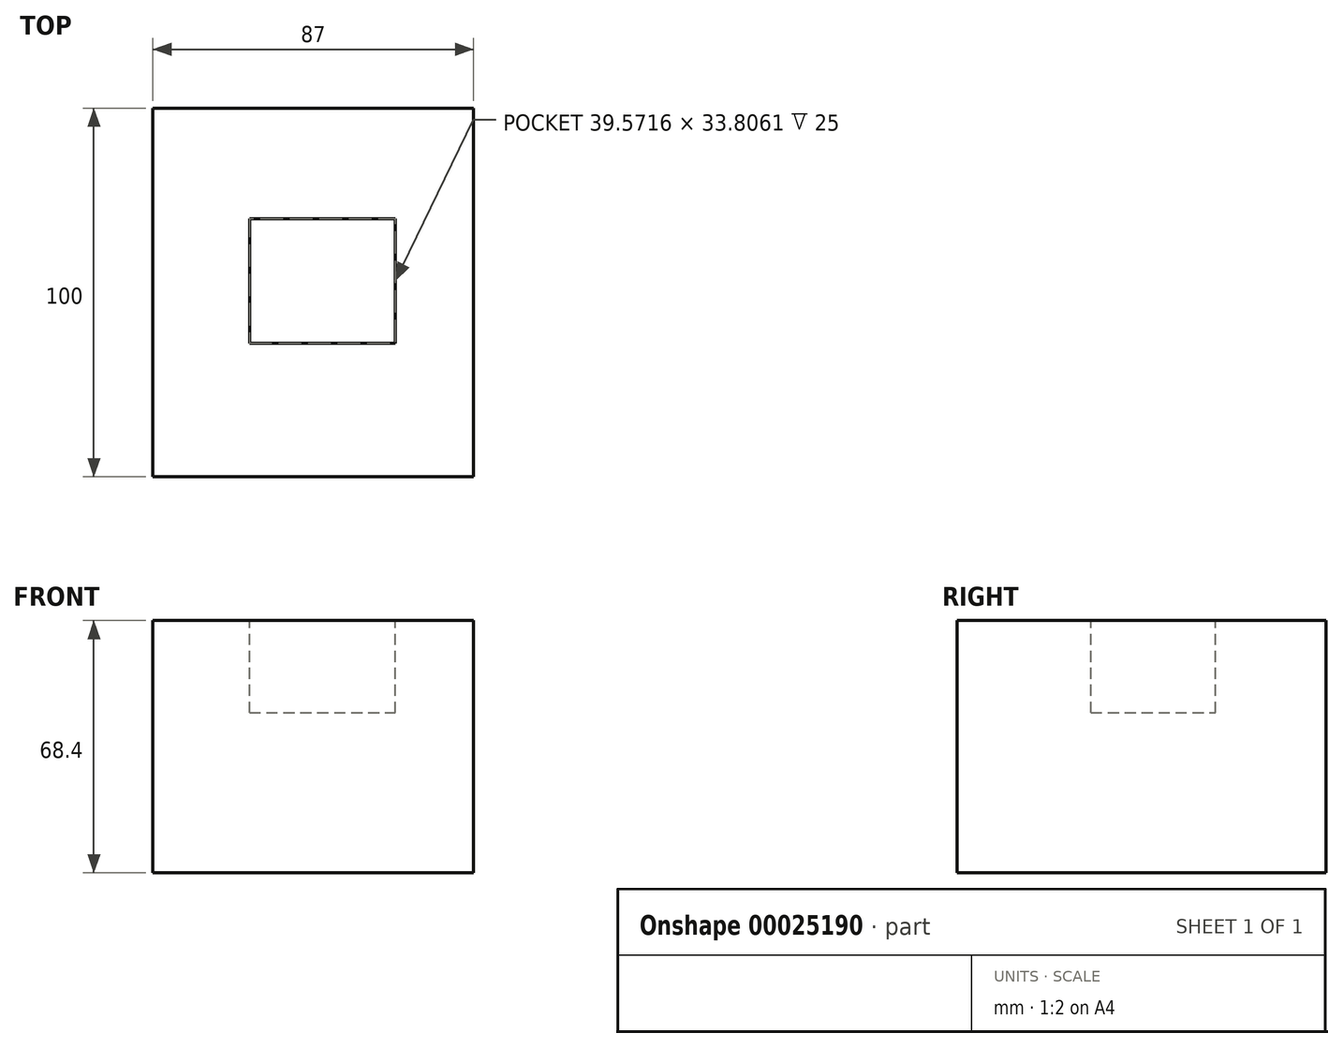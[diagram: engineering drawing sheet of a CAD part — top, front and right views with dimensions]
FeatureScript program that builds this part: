
annotation { "Feature Type Name" : "Feature", "Feature Type Description" : "" }
export const myFeature = defineFeature(function(context is Context, id is Id, definition is map)
    precondition{}
    {
        {
            var Q0;
            Q0=qCreatedBy(makeId("Front.planeOp"),FACE);
            var sketch = newSketch(context, id + "F0", { "sketchPlane" : qUnion([Q0])});
            skLineSegment(sketch, "E0.bottom", {"start": v(-44.81, -26.6) * mm, "end": v(42.2, -26.6) * mm});
            skLineSegment(sketch, "E0.top", {"start": v(-44.81, 41.8) * mm, "end": v(42.2, 41.8) * mm});
            skLineSegment(sketch, "E0.left", {"start": v(-44.81, -26.6) * mm, "end": v(-44.81, 41.8) * mm});
            skLineSegment(sketch, "E0.right", {"start": v(42.2, -26.6) * mm, "end": v(42.2, 41.8) * mm});
            skSolve(sketch);
        }
        {
            var Q0;
            Q0=makeQuery(id+"F0.imprint","IMPRINT",FACE,{"disambiguationData":[TD([[makeQuery(id+"F0.imprint","IMPRINT",EDGE,{"derivedFrom":sQuery(id+"F0.wireOp",EDGE,"E0.bottom")}),1.0]])]});
            extrude(context, id + "F1", {"entities" : qUnion([Q0]), "endBound" : BoundingType.SYMMETRIC, "depth" : 100 * mm});
        }
        {
            var Q0;
            Q0=makeQuery(id+"F1.opExtrude","SWEPT_FACE",FACE,{"disambiguationData":[OSD([sQuery(id+"F0.wireOp",EDGE,"E0.top")])]});
            var sketch = newSketch(context, id + "F2", { "sketchPlane" : qUnion([Q0])});
            skLineSegment(sketch, "E1.bottom", {"start": v(-18.6, -13.76) * mm, "end": v(20.97, -13.76) * mm});
            skLineSegment(sketch, "E1.top", {"start": v(-18.6, 20.05) * mm, "end": v(20.97, 20.05) * mm});
            skLineSegment(sketch, "E1.left", {"start": v(-18.6, -13.76) * mm, "end": v(-18.6, 20.05) * mm});
            skLineSegment(sketch, "E1.right", {"start": v(20.97, -13.76) * mm, "end": v(20.97, 20.05) * mm});
            skSolve(sketch);
        }
        {
            var Q0;
            Q0=makeQuery(id+"F2.imprint","IMPRINT",FACE,{"disambiguationData":[TD([[makeQuery(id+"F2.imprint","IMPRINT",EDGE,{"derivedFrom":sQuery(id+"F2.wireOp",EDGE,"E1.bottom")}),1.0]])]});
            extrude(context, id + "F3", {"entities" : qUnion([Q0]), "operationType" : NewBodyOperationType.REMOVE, "oppositeDirection" : true, "depth" : 25 * mm});
        }
    });
